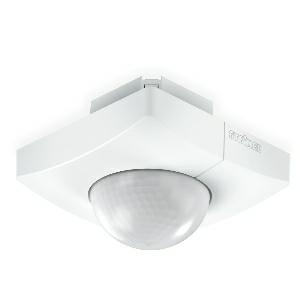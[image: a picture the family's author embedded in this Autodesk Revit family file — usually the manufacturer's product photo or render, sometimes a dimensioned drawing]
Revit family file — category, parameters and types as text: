
# Revit family: is_345_033804
name_source: partatom
category: Elektroinstallationen
revit_build: Autodesk Revit 2016 (Build: 20190508_0715(x64)
units: mm (PartAtom-declared; Revit-internal decimal feet)

## family parameters
Basisbauteil = Fläche
Beim Laden mit Abzugskörper schneiden = Nein
Bemaßung runder Anschluss = Durchmesser verwenden
Beschriftungsausrichtung beibehalten = Nein
Gemeinsam genutzt = Nein
Raumberechnungspunkt = Nein
Teiletyp = Normal

## types (1)
- IS 345
    Apparent Load = 0 VA
    Beschreibung = Type: Motion detectors; Dimensions (L x W x H): 78 x 94 x 94 mm; Mains power supply: 220 – 240 V / 50 – 60 Hz; Sensor Technology: passive infrared; Application, place: Indoors; Application, room: corridor / aisle, multi-storey / underground car park, Indoors; Installation site: ceiling; Installation: Concealed wiring; Switching zones: 280 switching zones; Electronic scalability: No; Mechanical scalability: No; Mounting height: 2,50 – 5,00 m; Optimum mounting height: 2,8 m; Detection angle: 360 °; Angle of aperture: 45 °; Sneak-by guard: Yes; Capability of masking out individual segments: Yes; Reach, radial: 12 x 6 m (72 m²); Reach, tangential: 23 x 6 m (138 m²); Twilight setting TEACH: Yes; Twilight setting: 2 – 1000 lx; Time setting: 5 sec – 15 min; Switching output 1, resistive: 2000 W; Switching output 1, number of LEDs / fluorescent lamps: 8 pcs.; Constant-lighting control: No; Basic light level function: No; Functions: Normal / test mode, Manual ON / ON-OFF; Settings via: Remote control, Potentiometers, Smart Remote; With remote control: No; Interconnection: Yes; IP-rating: IP20; Material: Plastic; Ambient temperature: -20 – 50 °C; Colour: white; Colour, RAL: 9003; Manufacturer's Warranty: 5 years; Version: COM1 - concealed, sq.; PU1, EAN: 4007841033804
    Height = 0 mm  [stored 0 ft]
    Hersteller = Steinel
    Length = 78 mm  [stored 0.255906 ft]
    Maximum range = 11.589 m
    ModVariant = Nein
    Modell = 033804
    Mounting Place = Ceiling
    Mounting Type = Recessed
    Number of Poles = 1
    OnlyDefault = Ja
    Power Factor = 1
    Product Name = IS 345
    Product group = Presence detector
    ProductGroupID = 4
    Protection Class = Protection class
    Protection Degree = IP 20
    RlxData = <blob elided: 137381 chars, md5=73f9f42a>
    Sensor characteristics = Stretched
    Sensor type = Passive (infrared)
    SensorDataFile = <blob elided: 5885 chars, md5=98bccc25>
    Type of entry = Motion
    Typenbild = produkt1_033804.jpg
    Typenkommentare = Product without accessories
    URL = http://relux.com
    VarID = ---
    Voltage = 0 V
    Vorgabe-Ansicht = 1800 mm
    Weight = 0.00 kg
    Width = 94 mm  [stored 0.308399 ft]

note: [stored X ft] marks values corroborated as IEEE doubles in the binary element streams (Revit-internal decimal feet)

## geometry (parser evidence)
native form markers: Sweep x15
no freeform markers — native parametric forms only
